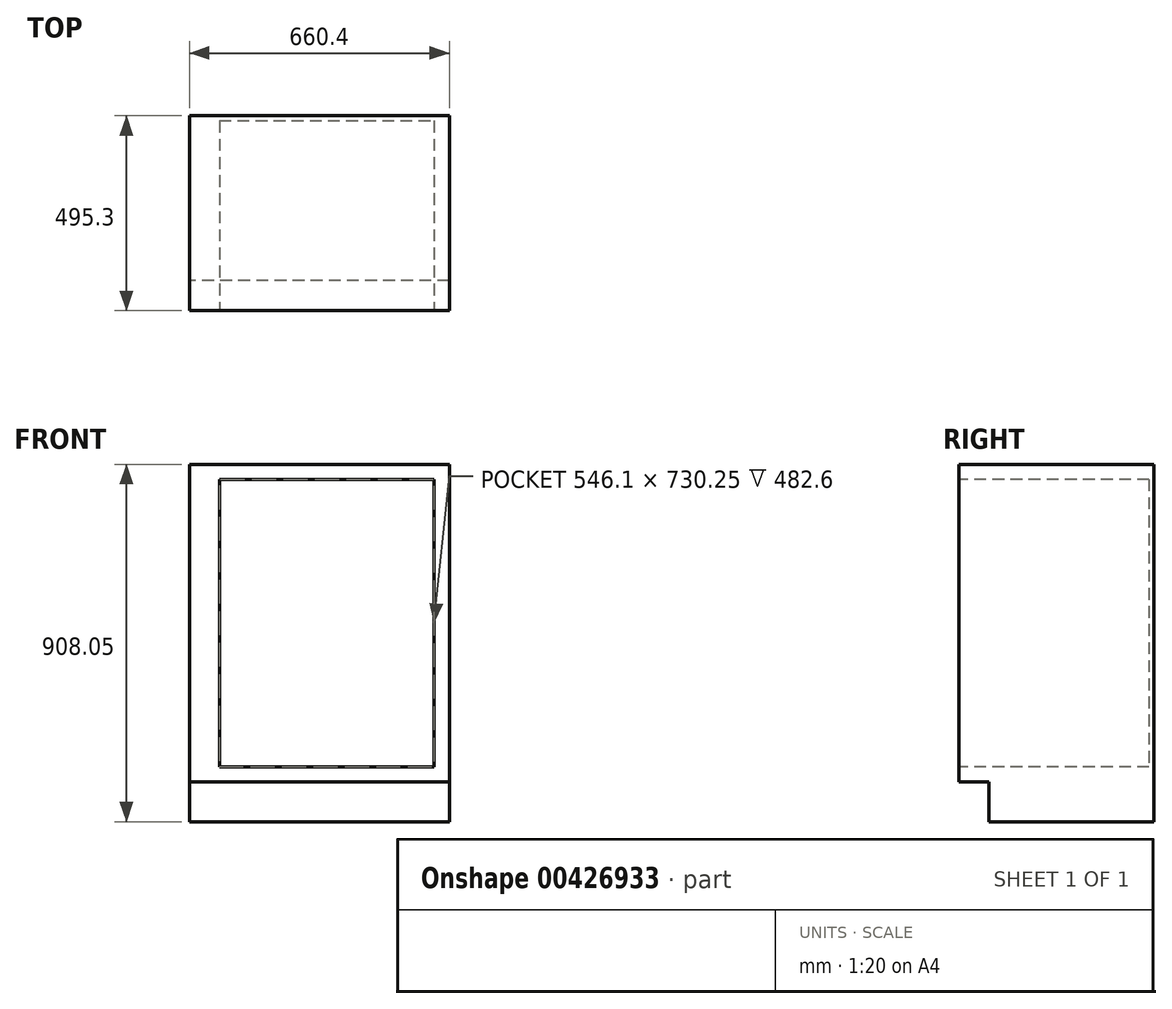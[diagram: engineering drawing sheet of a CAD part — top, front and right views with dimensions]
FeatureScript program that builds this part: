
annotation { "Feature Type Name" : "Feature", "Feature Type Description" : "" }
export const myFeature = defineFeature(function(context is Context, id is Id, definition is map)
    precondition{}
    {
        {
            var Q0;
            Q0=qCreatedBy(makeId("Right.planeOp"),FACE);
            var sketch = newSketch(context, id + "F0", { "sketchPlane" : qUnion([Q0])});
            skLineSegment(sketch, "E0", {"start": v(0, 0) * mm, "end": v(-419.1, 0) * mm});
            skLineSegment(sketch, "E1", {"start": v(-419.1, 0) * mm, "end": v(-419.1, 101.6) * mm});
            skLineSegment(sketch, "E2", {"start": v(-419.1, 101.6) * mm, "end": v(-495.3, 101.6) * mm});
            skLineSegment(sketch, "E3", {"start": v(-495.3, 101.6) * mm, "end": v(-495.3, 908.05) * mm});
            skLineSegment(sketch, "E4", {"start": v(-495.3, 908.05) * mm, "end": v(0, 908.05) * mm});
            skLineSegment(sketch, "E5", {"start": v(0, 908.05) * mm, "end": v(0, 0) * mm});
            skLineSegment(sketch, "E6", {"start": v(-419.1, 0) * mm, "end": v(-495.3, 0) * mm});
            skLineSegment(sketch, "E7", {"start": v(-495.3, 0) * mm, "end": v(-495.3, 101.6) * mm});
            skSolve(sketch);
        }
        {
            var Q0;
            Q0=makeQuery(id+"F0.imprint","IMPRINT",FACE,{"disambiguationData":[TD([[makeQuery(id+"F0.imprint","IMPRINT",EDGE,{"derivedFrom":sQuery(id+"F0.wireOp",EDGE,"E0")}),-1.0]])]});
            extrude(context, id + "F1", {"entities" : qUnion([Q0]), "depth" : 660.4 * mm});
        }
        {
            var Q0;
            Q0=makeQuery(id+"F1.opExtrude","SWEPT_FACE",FACE,{"disambiguationData":[OSD([sQuery(id+"F0.wireOp",EDGE,"E3")])]});
            var sketch = newSketch(context, id + "F2", { "sketchPlane" : qUnion([Q0])});
            skLineSegment(sketch, "E8.bottom", {"start": v(76.2, 869.95) * mm, "end": v(622.3, 869.95) * mm});
            skLineSegment(sketch, "E8.top", {"start": v(76.2, 139.7) * mm, "end": v(622.3, 139.7) * mm});
            skLineSegment(sketch, "E8.left", {"start": v(76.2, 869.95) * mm, "end": v(76.2, 139.7) * mm});
            skLineSegment(sketch, "E8.right", {"start": v(622.3, 869.95) * mm, "end": v(622.3, 139.7) * mm});
            skSolve(sketch);
        }
        {
            var Q0;
            Q0=makeQuery(id+"F2.imprint","IMPRINT",FACE,{"disambiguationData":[TD([[makeQuery(id+"F2.imprint","IMPRINT",EDGE,{"derivedFrom":sQuery(id+"F2.wireOp",EDGE,"E8.bottom")}),-1.0]])]});
            extrude(context, id + "F3", {"entities" : qUnion([Q0]), "operationType" : NewBodyOperationType.REMOVE, "oppositeDirection" : true, "depth" : 482.6 * mm});
        }
    });
